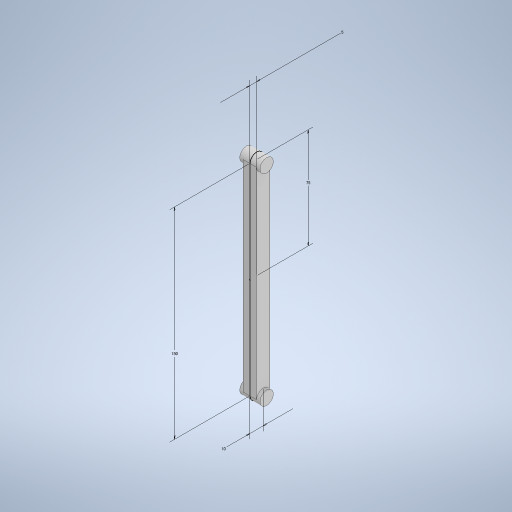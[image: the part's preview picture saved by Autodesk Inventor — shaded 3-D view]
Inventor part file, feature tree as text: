
AUTODESK INVENTOR PART (.ipt)
format: ipt  version: 2024.3 (Build 283343000, 343)  size: 252,928 bytes
history: native  units: mm
features: extrude x2, other x1, sketch x1
ambient origin geometry x8: Origin, YZ Plane, XZ Plane, XY Plane, X Axis, Y Axis, Z Axis, Center Point
bodies: Body1 (feature_tree)
feature tree (4):
  other  "ソリッド1"
  sketch  "スケッチ1"
  extrude  "押し出し1"  Depth=150.0mm
  extrude  "押し出し2"  Depth=10.0mm
